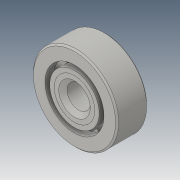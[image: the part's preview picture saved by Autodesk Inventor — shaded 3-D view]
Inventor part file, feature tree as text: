
AUTODESK INVENTOR PART (.ipt)
format: ipt  version: 2016 (Build 200138000, 138)  size: 508,928 bytes
history: native  units: in
note: dims shown in document units (in); Inventor stores cm internally (conversion verified against a paired STEP export)
features: other x10, revolve x4
ambient origin geometry x8: Origin, YZ Plane, XZ Plane, XY Plane, X Axis, Y Axis, Z Axis, Center Point
bodies: Solid1 (feature_tree), Solid2 (feature_tree), Solid3 (feature_tree), Solid4 (feature_tree), Solid5 (feature_tree), Solid6 (feature_tree), Solid7 (feature_tree), Solid8 (feature_tree), Solid9 (feature_tree), Solid10 (feature_tree), Solid11 (feature_tree), Solid12 (feature_tree), Solid13 (feature_tree)
feature tree (14):
  other  "6383K110_BALL BEARING.SLDPRT"
  revolve  "Revolve1"  [1 undecoded]
  revolve  "Revolve2"  [1 undecoded]
  revolve  "Revolve3"  [1 undecoded]
  revolve  "Revolve4"  [1 undecoded]
  other  "CirPattern1[1]"
  other  "CirPattern1[2]"
  other  "CirPattern1[3]"
  other  "CirPattern1[4]"
  other  "CirPattern1[5]"
  other  "CirPattern1[6]"
  other  "CirPattern1[7]"
  other  "CirPattern1[8]"
  other  "CirPattern1[9]"
note: 4 required parameter values undecoded (feature->parameter linkage not recoverable at this tier; creation-order binding heuristic only, values carry confidence <= 0.55)
